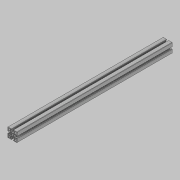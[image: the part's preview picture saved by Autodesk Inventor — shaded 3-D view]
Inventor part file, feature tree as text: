
AUTODESK INVENTOR PART (.ipt)
format: ipt  version: 2021.2 (Build 252289000, 289)  size: 200,704 bytes
history: native  units: in
note: dims shown in document units (in); Inventor stores cm internally (conversion verified against a paired STEP export)
features: other x2, extrude x1, sketch x1, projected_geometry x1
ambient origin geometry x8: Origin, YZ Plane, XZ Plane, XY Plane, X Axis, Y Axis, Z Axis, Center Point
bodies: Body1 (feature_tree)
feature tree (5):
  other  "ソリッド2"
  extrude  "押し出し1"  Depth=19.685in
  sketch  "スケッチ2"
  projected_geometry  "投影ループ1"
  other  "ソリッド1"
